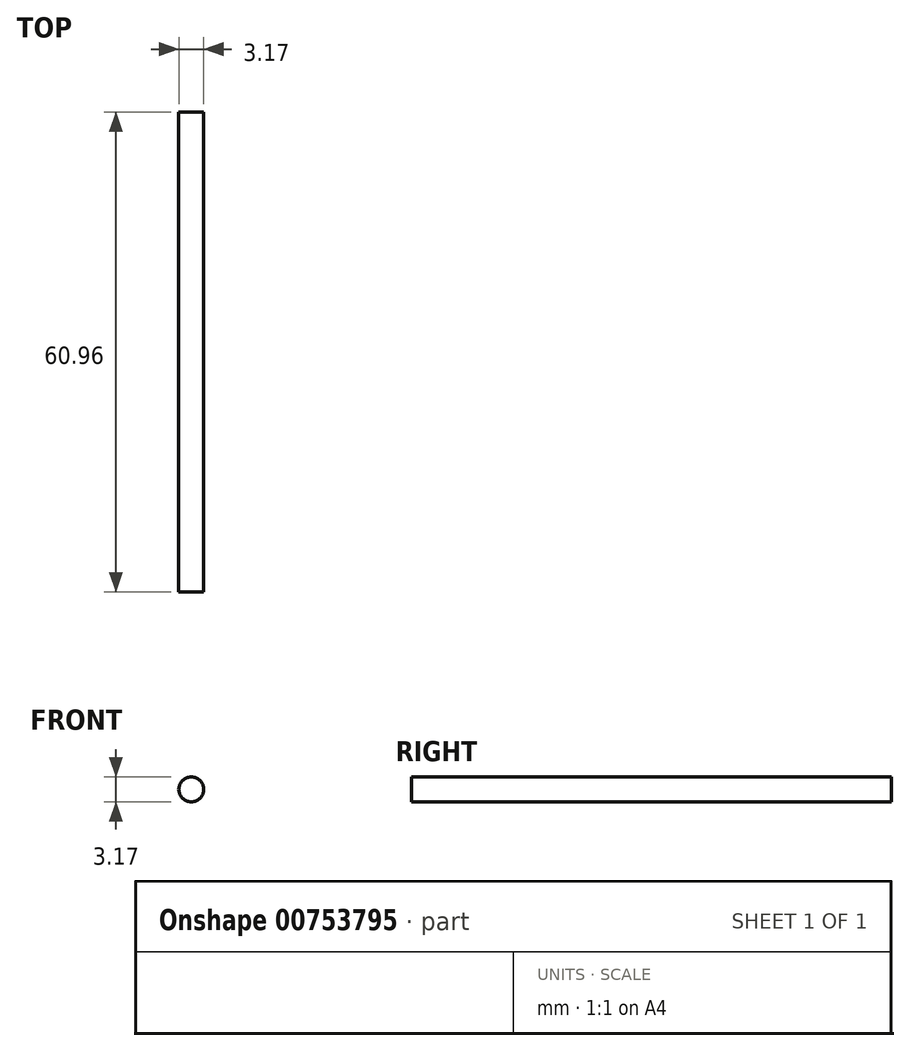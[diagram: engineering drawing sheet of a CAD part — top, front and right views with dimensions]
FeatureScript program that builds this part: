
annotation { "Feature Type Name" : "Feature", "Feature Type Description" : "" }
export const myFeature = defineFeature(function(context is Context, id is Id, definition is map)
    precondition{}
    {
        {
            var Q0;
            Q0=qCreatedBy(makeId("Front.planeOp"),FACE);
            var sketch = newSketch(context, id + "F0", { "sketchPlane" : qUnion([Q0])});
            skCircle(sketch, "E0", {"center": v(-52.8, 50.92) * mm, "radius": 1.59 * mm});
            skSolve(sketch);
        }
        {
            var Q0;
            Q0 = qSketchRegion(id + "F0", true);
            extrude(context, id + "F1", {"entities" : qUnion([Q0]), "depth" : 60.96 * mm, "offsetDistance" : 25.4 * mm});
        }
    });
